# Revit family: JC KONTAKTER JCK255 DE
name_source: partatom
category: Specialty Equipment
units: mm (PartAtom-declared; Revit-internal decimal feet)

## family parameters
Cut with Voids When Loaded = No
Enable Cutting in Views = Yes
Host = Face
Maintain Annotation Orientation = Yes
Part Type = Normal
Room Calculation Point = No
Round Connector Dimension = Use Diameter
Shared = No

## types (1)
- JCK255
    Anzahl der mikroschalter = 1
    CE-kennzeichnung = https://jckontakter.se
    Deckel = Aluminum 6060-T6 (schwarz)
    Default Elevation = 800 mm  [stored 2.62467 ft]
    Description = JCK255 ist nur 50 mm breit und wurde für die Montage an Glasflächen mit 50 mm Profilsystem sowie in anderen Bereichen entwickelt, in denen wenig Platz zur Verfügung steht. Das Modell ist aus schwarzeloxiertem Aluminium mit weißen Endkappen. gefertigt und verfügt über zwei taktile Rillen, die als zusätzliche Orientierungshilfe für sehbehinderte Personen dienen. So lässt sich leicht erfühlen, wo man drücken muss, um die Türöffnung zu aktivieren.
    Endkappen = POM Tenac C 4520 (weiss)
    Geringster nennstrom = 1mA/4 V DC
    Herstellungsland = Schweden
    Kern = Aluminum 6060-T6
    Manufacturer = JC kontakter
    Mikroschalter = Standard NO IP67
    Model = JCK255
    Nomineller nennstrom = 12 V - Resistive 6A Inductive L/R 5ms 6A, 24 V - Resistive 6A Inductive L/R 5ms 5A
    Produktgewicht = 0.263 kg.
    Technisches Produktblatt = https://grossflaechentaster.de
    URL = https://grossflaechentaster.de

note: [stored X ft] marks values corroborated as IEEE doubles in the binary element streams (Revit-internal decimal feet)

## geometry (parser evidence)
native form markers: Sweep x5
no freeform markers — native parametric forms only
